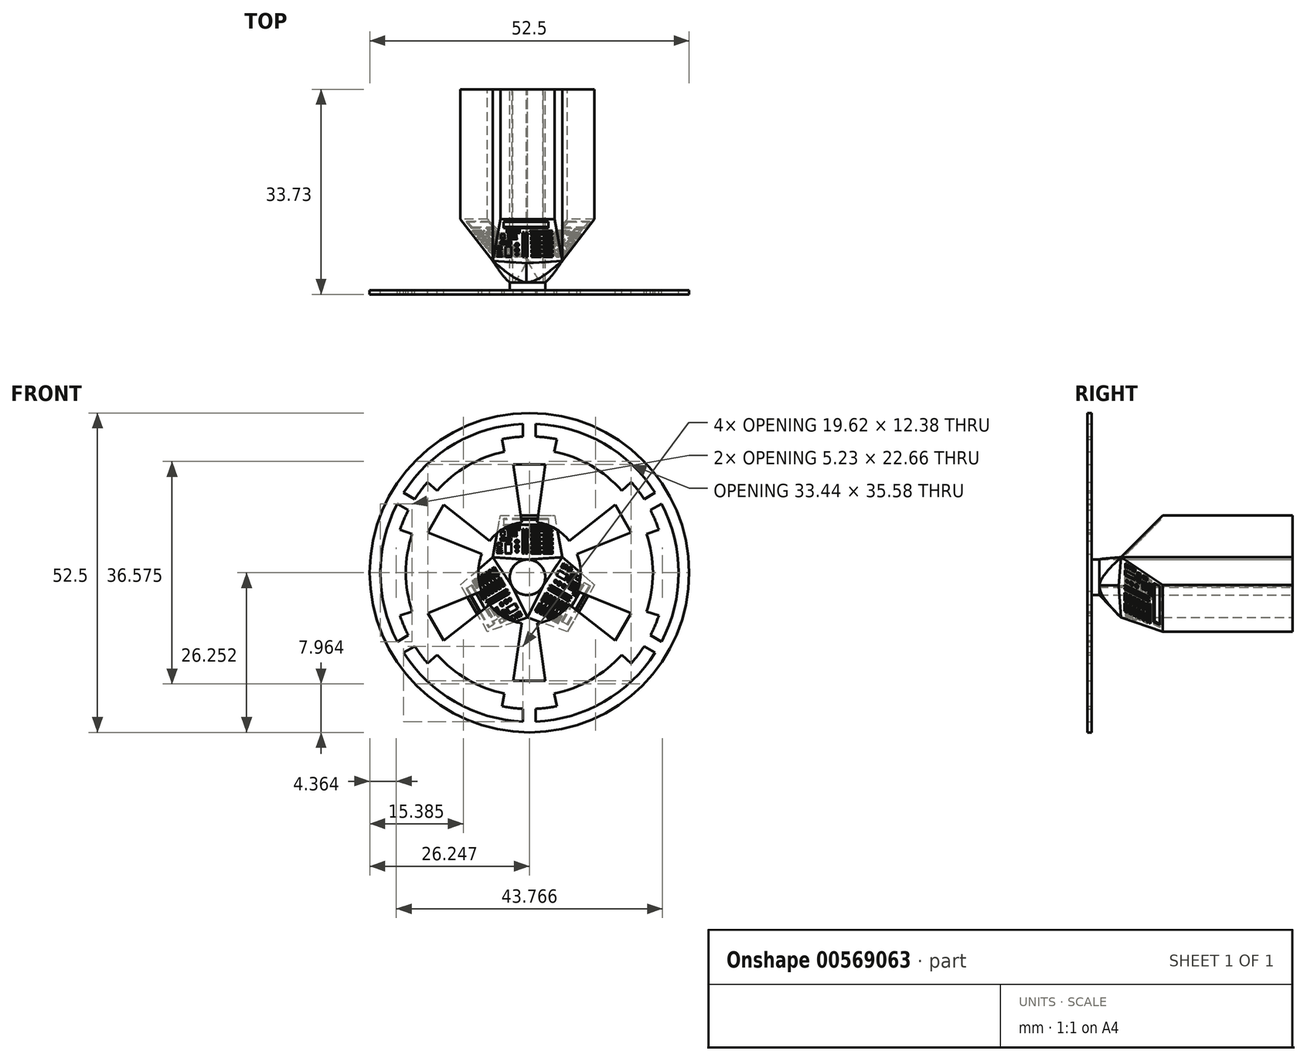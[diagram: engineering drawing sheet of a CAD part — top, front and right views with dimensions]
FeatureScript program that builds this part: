
annotation { "Feature Type Name" : "Feature", "Feature Type Description" : "" }
export const myFeature = defineFeature(function(context is Context, id is Id, definition is map)
    precondition{}
    {
        {
            var Q0;
            Q0=qCreatedBy(makeId("Front.planeOp"),FACE);
            var sketch = newSketch(context, id + "F0", { "sketchPlane" : qUnion([Q0])});
            skLineSegment(sketch, "E0", {"start": v(-5.73, 3.3) * mm, "end": v(-4.45, 10.16) * mm});
            skLineSegment(sketch, "E1", {"start": v(-4.45, 10.16) * mm, "end": v(0, 10.16) * mm});
            skLineSegment(sketch, "E2", {"start": v(0, 10.16) * mm, "end": v(4.45, 10.16) * mm});
            skLineSegment(sketch, "E3", {"start": v(4.45, 10.16) * mm, "end": v(5.73, 3.3) * mm});
            skLineSegment(sketch, "E4.1.0", {"start": v(0, -6.62) * mm, "end": v(-6.57, -8.93) * mm});
            skLineSegment(sketch, "E4.1.1", {"start": v(-6.57, -8.93) * mm, "end": v(-8.8, -5.08) * mm});
            skLineSegment(sketch, "E4.1.2", {"start": v(-8.8, -5.08) * mm, "end": v(-11.02, -1.23) * mm});
            skLineSegment(sketch, "E4.1.3", {"start": v(-11.02, -1.23) * mm, "end": v(-5.73, 3.3) * mm});
            skLineSegment(sketch, "E4.2.0", {"start": v(5.73, 3.3) * mm, "end": v(11.02, -1.23) * mm});
            skLineSegment(sketch, "E4.2.1", {"start": v(11.02, -1.23) * mm, "end": v(8.8, -5.08) * mm});
            skLineSegment(sketch, "E4.2.2", {"start": v(8.8, -5.08) * mm, "end": v(6.57, -8.93) * mm});
            skLineSegment(sketch, "E4.2.3", {"start": v(6.57, -8.93) * mm, "end": v(0, -6.62) * mm});
            skPoint(sketch, "E4.center", {"position": v(0, 0) * mm});
            skPoint(sketch, "E5.orphan", {"position": v(-3.18, 5.5) * mm});
            skPoint(sketch, "E6.end.orphan", {"position": v(-6.35, 0) * mm});
            skPoint(sketch, "E7.orphan", {"position": v(-3.18, -5.5) * mm});
            skPoint(sketch, "E8.orphan", {"position": v(3.17, 5.5) * mm});
            skPoint(sketch, "E9.orphan", {"position": v(6.35, 0) * mm});
            skCircle(sketch, "E10", {"center": v(0, 0) * mm, "radius": 2.92 * mm});
            skLineSegment(sketch, "E11", {"start": v(-5.73, 3.3) * mm, "end": v(-2.43, -1.63) * mm});
            skLineSegment(sketch, "E12", {"start": v(-2.43, -1.63) * mm, "end": v(0, -6.62) * mm});
            skLineSegment(sketch, "E13", {"start": v(0, -6.62) * mm, "end": v(2.62, -1.29) * mm});
            skLineSegment(sketch, "E14", {"start": v(2.62, -1.29) * mm, "end": v(5.73, 3.3) * mm});
            skLineSegment(sketch, "E15", {"start": v(5.73, 3.3) * mm, "end": v(0, 2.93) * mm});
            skLineSegment(sketch, "E16", {"start": v(0, 2.93) * mm, "end": v(-5.73, 3.3) * mm});
            skSolve(sketch);
        }
        {
            var Q0;
            {var subQ0=sQuery(id+"F0.wireOp",EDGE,"E10");var subQ1=makeQuery(id+"F0.imprint","INTERSECT",VERTEX,{"derivedFrom":[subQ0,sQuery(id+"F0.wireOp",EDGE,"E11"),sQuery(id+"F0.wireOp",EDGE,"E12")]});Q0=makeQuery(id+"F0.imprint","IMPRINT",FACE,{"disambiguationData":[TD([[makeQuery(id+"F0.imprint","IMPRINT",EDGE,{"disambiguationData":[TD([[subQ1,-1.0]])],"derivedFrom":subQ0}),1.0]])]});}
            extrude(context, id + "F1", {"entities" : qUnion([Q0]), "depth" : 33.02 * mm, "offsetDistance" : 25.4 * mm});
        }
        {
            var Q0;
            {var subQ0=sQuery(id+"F0.wireOp",EDGE,"E12");Q0=makeQuery(id+"F0.imprint","IMPRINT",FACE,{"disambiguationData":[TD([[makeQuery(id+"F0.imprint","IMPRINT",EDGE,{"derivedFrom":subQ0}),1.0]])]});}
            extrude(context, id + "F2", {"entities" : qUnion([Q0]), "depth" : 31.75 * mm, "offsetDistance" : 25.4 * mm});
        }
        {
            var Q0;
            Q0=makeQuery(id+"F0.imprint","IMPRINT",FACE,{"disambiguationData":[TD([[makeQuery(id+"F0.imprint","IMPRINT",EDGE,{"derivedFrom":sQuery(id+"F0.wireOp",EDGE,"E0")}),-1.0]])]});
            extrude(context, id + "F3", {"entities" : qUnion([Q0]), "depth" : 28.57 * mm, "offsetDistance" : 25.4 * mm});
        }
        {
            var Q0;
            Q0=makeQuery(id+"F3.opExtrude","CAP_EDGE",EDGE,{"disambiguationData":[OSD([sQuery(id+"F0.wireOp",EDGE,"E1"),sQuery(id+"F0.wireOp",EDGE,"E2")])],"isStart":false});
            cPoint(context, id + "F4", {"entities" : qUnion([Q0]), "parameter" : 0.5});
        }
        {
            var Q0;
            Q0=makeQuery(id+"F3.opExtrude","CAP_VERTEX",VERTEX,{"disambiguationData":[OSD([sQuery(id+"F0.wireOp",EDGE,"E15"),sQuery(id+"F0.wireOp",EDGE,"E16")])],"isStart":false});
            var Q1;
            Q1 = qCreatedBy(id + "F4" ,VERTEX);
            var Q2;
            Q2=sQuery(id+"F0.wireOp",VERTEX,"E15.end");
            cPlane(context, id + "F5", {"entities" : qUnion([Q0, Q1, Q2]), "cplaneType" : CPlaneType.THREE_POINT, "offset" : 25.4 * mm, "width" : 152.4 * mm, "height" : 152.4 * mm});
        }
        {
            var Q0;
            Q0=qCreatedBy(id+"F5.planeOp",FACE);
            var sketch = newSketch(context, id + "F6", { "sketchPlane" : qUnion([Q0])});
            skLineSegment(sketch, "E17", {"start": v(-28.58, 2.93) * mm, "end": v(-28.58, 10.16) * mm});
            skLineSegment(sketch, "E18", {"start": v(-28.58, 10.16) * mm, "end": v(-21.34, 10.16) * mm});
            skLineSegment(sketch, "E19", {"start": v(-21.34, 10.16) * mm, "end": v(-28.58, 2.93) * mm});
            skSolve(sketch);
        }
        {
            var Q0;
            Q0 = qSketchRegion(id + "F6", true);
            extrude(context, id + "F7", {"entities" : qUnion([Q0]), "operationType" : NewBodyOperationType.REMOVE, "endBound" : BoundingType.SYMMETRIC, "oppositeDirection" : true, "depth" : 25.4 * mm, "offsetDistance" : 25.4 * mm});
        }
        {
            var Q0;
            Q0=makeQuery(id+"F7.boolean.opBoolean","COPY",FACE,{"derivedFrom":makeQuery(id+"F7.opExtrude","SWEPT_FACE",FACE,{"disambiguationData":[OSD([sQuery(id+"F6.wireOp",EDGE,"E19")])]})});
            var sketch = newSketch(context, id + "F8", { "sketchPlane" : qUnion([Q0])});
            skLineSegment(sketch, "E20.bottom", {"start": v(4.16, -16.74) * mm, "end": v(2.61, -16.74) * mm});
            skLineSegment(sketch, "E20.top", {"start": v(4.16, -16.07) * mm, "end": v(2.61, -16.07) * mm});
            skLineSegment(sketch, "E20.left", {"start": v(4.16, -16.74) * mm, "end": v(4.16, -16.07) * mm});
            skLineSegment(sketch, "E20.right", {"start": v(2.61, -16.74) * mm, "end": v(2.61, -16.07) * mm});
            skLineSegment(sketch, "E21.bottom", {"start": v(-2.69, -16.71) * mm, "end": v(-3.61, -16.71) * mm});
            skLineSegment(sketch, "E21.top", {"start": v(-2.69, -14.27) * mm, "end": v(-3.61, -14.27) * mm});
            skLineSegment(sketch, "E21.left", {"start": v(-2.69, -16.71) * mm, "end": v(-2.69, -14.27) * mm});
            skLineSegment(sketch, "E21.right", {"start": v(-3.61, -16.71) * mm, "end": v(-3.61, -14.27) * mm});
            skCircle(sketch, "E22", {"center": v(-1.84, -12.51) * mm, "radius": 0.13 * mm});
            skLineSegment(sketch, "E23.1.0.0", {"start": v(4.14, -15.75) * mm, "end": v(2.6, -15.75) * mm});
            skLineSegment(sketch, "E23.1.0.1", {"start": v(2.6, -15.75) * mm, "end": v(2.6, -15.07) * mm});
            skLineSegment(sketch, "E23.1.0.2", {"start": v(4.14, -15.07) * mm, "end": v(2.6, -15.07) * mm});
            skLineSegment(sketch, "E23.1.0.3", {"start": v(4.14, -15.75) * mm, "end": v(4.14, -15.07) * mm});
            skLineSegment(sketch, "E23.2.0.0", {"start": v(4.12, -14.75) * mm, "end": v(2.57, -14.75) * mm});
            skLineSegment(sketch, "E23.2.0.1", {"start": v(2.57, -14.75) * mm, "end": v(2.57, -14.08) * mm});
            skLineSegment(sketch, "E23.2.0.2", {"start": v(4.12, -14.08) * mm, "end": v(2.57, -14.08) * mm});
            skLineSegment(sketch, "E23.2.0.3", {"start": v(4.12, -14.75) * mm, "end": v(4.12, -14.08) * mm});
            skLineSegment(sketch, "E23.3.0.0", {"start": v(4.1, -13.76) * mm, "end": v(2.55, -13.76) * mm});
            skLineSegment(sketch, "E23.3.0.1", {"start": v(2.55, -13.76) * mm, "end": v(2.55, -13.08) * mm});
            skLineSegment(sketch, "E23.3.0.2", {"start": v(4.1, -13.08) * mm, "end": v(2.55, -13.08) * mm});
            skLineSegment(sketch, "E23.3.0.3", {"start": v(4.1, -13.76) * mm, "end": v(4.1, -13.08) * mm});
            skLineSegment(sketch, "E23.4.0.0", {"start": v(4.09, -12.77) * mm, "end": v(2.53, -12.77) * mm});
            skLineSegment(sketch, "E23.4.0.1", {"start": v(2.53, -12.77) * mm, "end": v(2.53, -12.1) * mm});
            skLineSegment(sketch, "E23.4.0.2", {"start": v(4.09, -12.1) * mm, "end": v(2.53, -12.1) * mm});
            skLineSegment(sketch, "E23.4.0.3", {"start": v(4.09, -12.77) * mm, "end": v(4.09, -12.1) * mm});
            skLineSegment(sketch, "E23.direction1", {"start": v(2.61, -16.74) * mm, "end": v(2.6, -15.75) * mm, "construction": true});
            skLineSegment(sketch, "E24.1.0.0", {"start": v(0.58, -12.76) * mm, "end": v(0.58, -12.09) * mm});
            skLineSegment(sketch, "E24.1.0.1", {"start": v(2.14, -12.09) * mm, "end": v(0.58, -12.09) * mm});
            skLineSegment(sketch, "E24.1.0.2", {"start": v(0.64, -15.74) * mm, "end": v(0.64, -15.07) * mm});
            skLineSegment(sketch, "E24.1.0.3", {"start": v(2.2, -15.74) * mm, "end": v(2.2, -15.07) * mm});
            skLineSegment(sketch, "E24.1.0.4", {"start": v(2.21, -16.74) * mm, "end": v(2.21, -16.06) * mm});
            skLineSegment(sketch, "E24.1.0.5", {"start": v(2.2, -15.07) * mm, "end": v(0.64, -15.07) * mm});
            skLineSegment(sketch, "E24.1.0.6", {"start": v(2.21, -16.06) * mm, "end": v(0.66, -16.06) * mm});
            skLineSegment(sketch, "E24.1.0.7", {"start": v(0.66, -16.74) * mm, "end": v(0.64, -15.74) * mm, "construction": true});
            skLineSegment(sketch, "E24.1.0.8", {"start": v(2.21, -16.74) * mm, "end": v(0.66, -16.74) * mm});
            skLineSegment(sketch, "E24.1.0.9", {"start": v(2.17, -14.75) * mm, "end": v(2.17, -14.08) * mm});
            skLineSegment(sketch, "E24.1.0.10", {"start": v(2.15, -13.08) * mm, "end": v(0.6, -13.08) * mm});
            skLineSegment(sketch, "E24.1.0.11", {"start": v(2.17, -14.75) * mm, "end": v(0.62, -14.75) * mm});
            skLineSegment(sketch, "E24.1.0.12", {"start": v(2.15, -13.76) * mm, "end": v(0.6, -13.76) * mm});
            skLineSegment(sketch, "E24.1.0.13", {"start": v(0.62, -14.75) * mm, "end": v(0.62, -14.08) * mm});
            skLineSegment(sketch, "E24.1.0.14", {"start": v(2.15, -13.76) * mm, "end": v(2.15, -13.08) * mm});
            skLineSegment(sketch, "E24.1.0.15", {"start": v(2.14, -12.76) * mm, "end": v(0.58, -12.76) * mm});
            skLineSegment(sketch, "E24.1.0.16", {"start": v(2.14, -12.76) * mm, "end": v(2.14, -12.09) * mm});
            skLineSegment(sketch, "E24.1.0.17", {"start": v(2.17, -14.08) * mm, "end": v(0.62, -14.08) * mm});
            skLineSegment(sketch, "E24.1.0.18", {"start": v(0.6, -13.76) * mm, "end": v(0.6, -13.08) * mm});
            skLineSegment(sketch, "E24.1.0.19", {"start": v(2.2, -15.74) * mm, "end": v(0.64, -15.74) * mm});
            skLineSegment(sketch, "E24.1.0.20", {"start": v(0.66, -16.74) * mm, "end": v(0.66, -16.06) * mm});
            skLineSegment(sketch, "E24.direction1", {"start": v(2.61, -16.74) * mm, "end": v(0.66, -16.74) * mm, "construction": true});
            skCircle(sketch, "E25.1.0.0", {"center": v(-2.15, -12.52) * mm, "radius": 0.13 * mm});
            skCircle(sketch, "E25.2.0.0", {"center": v(-2.46, -12.52) * mm, "radius": 0.13 * mm});
            skCircle(sketch, "E25.3.0.0", {"center": v(-2.76, -12.52) * mm, "radius": 0.13 * mm});
            skCircle(sketch, "E25.4.0.0", {"center": v(-3.07, -12.52) * mm, "radius": 0.13 * mm});
            skLineSegment(sketch, "E25.direction1", {"start": v(-1.84, -12.51) * mm, "end": v(-2.15, -12.52) * mm, "construction": true});
            skCircle(sketch, "E26.1.0.0", {"center": v(-2.8, -12.14) * mm, "radius": 0.13 * mm});
            skCircle(sketch, "E26.1.0.1", {"center": v(-2.18, -12.13) * mm, "radius": 0.13 * mm});
            skCircle(sketch, "E26.1.0.2", {"center": v(-2.48, -12.14) * mm, "radius": 0.13 * mm});
            skCircle(sketch, "E26.1.0.3", {"center": v(-1.87, -12.13) * mm, "radius": 0.13 * mm});
            skLineSegment(sketch, "E26.1.0.4", {"start": v(-1.87, -12.13) * mm, "end": v(-2.18, -12.13) * mm, "construction": true});
            skCircle(sketch, "E26.1.0.5", {"center": v(-3.1, -12.14) * mm, "radius": 0.13 * mm});
            skCircle(sketch, "E26.2.0.0", {"center": v(-2.82, -11.76) * mm, "radius": 0.13 * mm});
            skCircle(sketch, "E26.2.0.1", {"center": v(-2.2, -11.75) * mm, "radius": 0.13 * mm});
            skCircle(sketch, "E26.2.0.2", {"center": v(-2.5, -11.75) * mm, "radius": 0.13 * mm});
            skCircle(sketch, "E26.2.0.3", {"center": v(-1.9, -11.75) * mm, "radius": 0.13 * mm});
            skLineSegment(sketch, "E26.2.0.4", {"start": v(-1.9, -11.75) * mm, "end": v(-2.2, -11.75) * mm, "construction": true});
            skCircle(sketch, "E26.2.0.5", {"center": v(-3.13, -11.76) * mm, "radius": 0.13 * mm});
            skLineSegment(sketch, "E26.direction1", {"start": v(-3.07, -12.52) * mm, "end": v(-3.1, -12.14) * mm, "construction": true});
            skLineSegment(sketch, "E27.bottom", {"start": v(0, -16.72) * mm, "end": v(-0.28, -16.72) * mm});
            skLineSegment(sketch, "E27.top", {"start": v(0, -11.05) * mm, "end": v(-0.28, -11.05) * mm});
            skLineSegment(sketch, "E27.left", {"start": v(0, -16.72) * mm, "end": v(0, -11.05) * mm});
            skLineSegment(sketch, "E27.right", {"start": v(-0.28, -16.72) * mm, "end": v(-0.28, -11.05) * mm});
            skLineSegment(sketch, "E28.bottom", {"start": v(-0.56, -16.73) * mm, "end": v(-0.84, -16.73) * mm});
            skLineSegment(sketch, "E28.top", {"start": v(-0.56, -11.05) * mm, "end": v(-0.84, -11.05) * mm});
            skLineSegment(sketch, "E28.left", {"start": v(-0.56, -16.73) * mm, "end": v(-0.56, -11.05) * mm});
            skLineSegment(sketch, "E28.right", {"start": v(-0.84, -16.73) * mm, "end": v(-0.84, -11.05) * mm});
            skLineSegment(sketch, "E29.bottom", {"start": v(4.1, -11.55) * mm, "end": v(0.43, -11.55) * mm});
            skLineSegment(sketch, "E29.top", {"start": v(4.1, -11.28) * mm, "end": v(0.43, -11.28) * mm});
            skLineSegment(sketch, "E29.left", {"start": v(4.1, -11.55) * mm, "end": v(4.1, -11.28) * mm});
            skLineSegment(sketch, "E29.right", {"start": v(0.43, -11.55) * mm, "end": v(0.43, -11.28) * mm});
            skLineSegment(sketch, "E30.bottom", {"start": v(4.05, -10.93) * mm, "end": v(0.42, -10.93) * mm});
            skLineSegment(sketch, "E30.top", {"start": v(4.05, -10.71) * mm, "end": v(0.42, -10.71) * mm});
            skLineSegment(sketch, "E30.left", {"start": v(4.05, -10.93) * mm, "end": v(4.05, -10.71) * mm});
            skLineSegment(sketch, "E30.right", {"start": v(0.42, -10.93) * mm, "end": v(0.42, -10.71) * mm});
            skCircle(sketch, "E31", {"center": v(-1.73, -16.14) * mm, "radius": 0.25 * mm});
            skCircle(sketch, "E32", {"center": v(-1.71, -15.13) * mm, "radius": 0.36 * mm});
            skCircle(sketch, "E33", {"center": v(-1.73, -13.91) * mm, "radius": 0.34 * mm});
            skLineSegment(sketch, "E34.bottom", {"start": v(-4.15, -16.61) * mm, "end": v(-5, -16.61) * mm});
            skLineSegment(sketch, "E34.top", {"start": v(-4.15, -16.35) * mm, "end": v(-5, -16.35) * mm});
            skLineSegment(sketch, "E34.left", {"start": v(-4.15, -16.61) * mm, "end": v(-4.15, -16.35) * mm});
            skLineSegment(sketch, "E34.right", {"start": v(-5, -16.61) * mm, "end": v(-5, -16.35) * mm});
            skLineSegment(sketch, "E35.bottom", {"start": v(-4.18, -16.14) * mm, "end": v(-4.98, -16.14) * mm});
            skLineSegment(sketch, "E35.top", {"start": v(-4.18, -15.9) * mm, "end": v(-4.98, -15.9) * mm});
            skLineSegment(sketch, "E35.left", {"start": v(-4.18, -16.14) * mm, "end": v(-4.18, -15.9) * mm});
            skLineSegment(sketch, "E35.right", {"start": v(-4.98, -16.14) * mm, "end": v(-4.98, -15.9) * mm});
            skLineSegment(sketch, "E36.bottom", {"start": v(-4.24, -15.63) * mm, "end": v(-5.01, -15.63) * mm});
            skLineSegment(sketch, "E36.top", {"start": v(-4.24, -15.45) * mm, "end": v(-5.01, -15.45) * mm});
            skLineSegment(sketch, "E36.left", {"start": v(-4.24, -15.63) * mm, "end": v(-4.24, -15.45) * mm});
            skLineSegment(sketch, "E36.right", {"start": v(-5.01, -15.63) * mm, "end": v(-5.01, -15.45) * mm});
            skLineSegment(sketch, "E37.bottom", {"start": v(-4.23, -15.14) * mm, "end": v(-4.93, -15.14) * mm});
            skLineSegment(sketch, "E37.top", {"start": v(-4.23, -14.22) * mm, "end": v(-4.93, -14.22) * mm});
            skLineSegment(sketch, "E37.left", {"start": v(-4.23, -15.14) * mm, "end": v(-4.23, -14.22) * mm});
            skLineSegment(sketch, "E37.right", {"start": v(-4.93, -15.14) * mm, "end": v(-4.93, -14.22) * mm});
            skLineSegment(sketch, "E38.bottom", {"start": v(3.45, -8.6) * mm, "end": v(-3.9, -8.6) * mm});
            skLineSegment(sketch, "E38.top", {"start": v(3.45, -10.02) * mm, "end": v(-3.9, -10.02) * mm});
            skLineSegment(sketch, "E38.left", {"start": v(3.45, -8.6) * mm, "end": v(3.45, -10.02) * mm});
            skLineSegment(sketch, "E38.right", {"start": v(-3.9, -8.6) * mm, "end": v(-3.9, -10.02) * mm});
            skLineSegment(sketch, "E39.bottom", {"start": v(-3.77, -12.52) * mm, "end": v(-4.38, -12.52) * mm});
            skLineSegment(sketch, "E39.top", {"start": v(-3.77, -11.43) * mm, "end": v(-4.38, -11.43) * mm});
            skLineSegment(sketch, "E39.left", {"start": v(-3.77, -12.52) * mm, "end": v(-3.77, -11.43) * mm});
            skLineSegment(sketch, "E39.right", {"start": v(-4.38, -12.52) * mm, "end": v(-4.38, -11.43) * mm});
            skLineSegment(sketch, "E40.bottom", {"start": v(-1.29, -10.31) * mm, "end": v(-3.43, -10.31) * mm});
            skLineSegment(sketch, "E40.top", {"start": v(-1.29, -11.18) * mm, "end": v(-3.43, -11.18) * mm});
            skLineSegment(sketch, "E40.left", {"start": v(-1.29, -10.31) * mm, "end": v(-1.29, -11.18) * mm});
            skLineSegment(sketch, "E40.right", {"start": v(-3.43, -10.31) * mm, "end": v(-3.43, -11.18) * mm});
            skLineSegment(sketch, "E41.bottom", {"start": v(-2.63, -13.76) * mm, "end": v(-4.45, -13.76) * mm});
            skLineSegment(sketch, "E41.top", {"start": v(-2.63, -13.07) * mm, "end": v(-4.45, -13.07) * mm});
            skLineSegment(sketch, "E41.left", {"start": v(-2.63, -13.76) * mm, "end": v(-2.63, -13.07) * mm});
            skLineSegment(sketch, "E41.right", {"start": v(-4.45, -13.76) * mm, "end": v(-4.45, -13.07) * mm});
            skSolve(sketch);
        }
        {
            var Q0;
            Q0 = qSketchRegion(id + "F8", true);
            extrude(context, id + "F9", {"entities" : qUnion([Q0]), "operationType" : NewBodyOperationType.REMOVE, "oppositeDirection" : true, "depth" : 0.25 * mm, "offsetDistance" : 25.4 * mm});
        }
        {
            var Q0;
            Q0=makeQuery(id+"F3.opExtrude","SWEPT_BODY",BODY,{"disambiguationData":[OSD([sQuery(id+"F0.wireOp",EDGE,"E0"),sQuery(id+"F0.wireOp",EDGE,"E1"),sQuery(id+"F0.wireOp",EDGE,"E2"),sQuery(id+"F0.wireOp",EDGE,"E3"),sQuery(id+"F0.wireOp",EDGE,"E15"),sQuery(id+"F0.wireOp",EDGE,"E16")])]});
            var Q1;
            Q1=makeQuery(id+"F1.opExtrude","SWEPT_BODY",BODY,{"disambiguationData":[OSD([sQuery(id+"F0.wireOp",EDGE,"E10")])]});
            var Q2;
            Q2=makeQuery(id+"F1.opExtrude","SWEPT_FACE",FACE,{"disambiguationData":[OSD([sQuery(id+"F0.wireOp",EDGE,"E10")])]});
            circularPattern(context, id + "F10", {"entities" : qUnion([Q0, Q1]), "axis" : qUnion([Q2]), "angle" : 360 * degree, "instanceCount" : 3, "equalSpace" : true});
        }
        {
            var Q0;
            Q0=makeQuery(id+"F2.opExtrude","SWEPT_BODY",BODY,{"disambiguationData":[OSD([sQuery(id+"F0.wireOp",EDGE,"E10"),sQuery(id+"F0.wireOp",EDGE,"E12"),sQuery(id+"F0.wireOp",EDGE,"E13")])]});
            var Q1;
            Q1=makeQuery(id+"F10.opPattern","COPY",FACE,{"derivedFrom":makeQuery(id+"F1.opExtrude","SWEPT_FACE",FACE,{"disambiguationData":[OSD([sQuery(id+"F0.wireOp",EDGE,"E10")])]}),"instanceName":"1"});
            circularPattern(context, id + "F11", {"entities" : qUnion([Q0]), "axis" : qUnion([Q1]), "angle" : 360 * degree, "instanceCount" : 3, "equalSpace" : true});
        }
        {
            var Q0;
            Q0=qCreatedBy(id+"F5.planeOp",FACE);
            var sketch = newSketch(context, id + "F12", { "sketchPlane" : qUnion([Q0])});
            skLineSegment(sketch, "E42", {"start": v(-31.75, -6.62) * mm, "end": v(-28.2, -6.62) * mm});
            skLineSegment(sketch, "E43", {"start": v(-28.2, -6.62) * mm, "end": v(-31.75, -2.91) * mm});
            skLineSegment(sketch, "E44", {"start": v(-31.75, -2.91) * mm, "end": v(-31.75, -6.62) * mm});
            skSolve(sketch);
        }
        {
            var Q0;
            Q0 = qSketchRegion(id + "F12", true);
            var Q1;
            Q1=makeQuery(id+"F10.opPattern","COPY",FACE,{"derivedFrom":makeQuery(id+"F1.opExtrude","SWEPT_FACE",FACE,{"disambiguationData":[OSD([sQuery(id+"F0.wireOp",EDGE,"E10")])]}),"instanceName":"1"});
            revolve(context, id + "F13", {"operationType" : NewBodyOperationType.REMOVE, "entities" : qUnion([Q0]), "axis" : qUnion([Q1]), "revolveType" : RevolveType.FULL, "oppositeDirection" : true});
        }
        {
            var Q0;
            Q0=makeQuery(id+"F1.opExtrude","CAP_FACE",FACE,{"disambiguationData":[OSD([sQuery(id+"F0.wireOp",EDGE,"E10")])],"isStart":false});
            var sketch = newSketch(context, id + "F14", { "sketchPlane" : qUnion([Q0])});
            skArc(sketch, "E45", {"start": v(0.45, 38.59) * mm, "mid": v(-35.26, 12.53) * mm, "end": v(-21.35, -29.42) * mm});
            skArc(sketch, "E46", {"start": v(-30.58, 17.27) * mm, "mid": v(-34.55, 1.09) * mm, "end": v(-30.58, -15.1) * mm});
            skLineSegment(sketch, "E47.left", {"start": v(-1.05, 36.07) * mm, "end": v(-1.05, 33.05) * mm});
            skLineSegment(sketch, "E47.right", {"start": v(1.95, 36.07) * mm, "end": v(1.95, 33.05) * mm});
            skLineSegment(sketch, "E48.1.0", {"start": v(-30.58, -15.1) * mm, "end": v(-27.98, -13.6) * mm});
            skLineSegment(sketch, "E48.1.1", {"start": v(-29.08, -17.7) * mm, "end": v(-26.48, -16.2) * mm});
            skLineSegment(sketch, "E48.2.0", {"start": v(29.99, -17.7) * mm, "end": v(27.39, -16.2) * mm});
            skLineSegment(sketch, "E48.2.1", {"start": v(31.49, -15.1) * mm, "end": v(28.89, -13.6) * mm});
            skArc(sketch, "E49", {"start": v(-27.98, 15.77) * mm, "mid": v(-28.92, 13.8) * mm, "end": v(-29.72, 11.75) * mm});
            skArc(sketch, "E50", {"start": v(-27.07, 10.22) * mm, "mid": v(-28.55, 1.09) * mm, "end": v(-27.07, -8.05) * mm});
            skPoint(sketch, "E51.orphan", {"position": v(-31.47, 17.79) * mm});
            skPoint(sketch, "E52.orphan", {"position": v(-29.97, 20.39) * mm});
            skPoint(sketch, "E53.orphan", {"position": v(-27.8, 24.15) * mm});
            skLineSegment(sketch, "E54.trimOffspring", {"start": v(-26.48, 18.37) * mm, "end": v(-29.08, 19.87) * mm});
            skLineSegment(sketch, "E55.trimOffspring", {"start": v(-27.98, 15.77) * mm, "end": v(-30.58, 17.27) * mm});
            skArc(sketch, "E56.trimOffspring", {"start": v(-29.72, -9.58) * mm, "mid": v(-28.92, -11.62) * mm, "end": v(-27.98, -13.6) * mm});
            skArc(sketch, "E57.trimOffspring", {"start": v(-23.87, 21.88) * mm, "mid": v(-25.23, 20.17) * mm, "end": v(-26.48, 18.37) * mm});
            skPoint(sketch, "E58.orphan", {"position": v(-5.4, 37.09) * mm});
            skPoint(sketch, "E59.orphan", {"position": v(1.95, 37.09) * mm});
            skPoint(sketch, "E60.orphan", {"position": v(-1.05, 37.09) * mm});
            skPoint(sketch, "E61.orphan", {"position": v(6.3, 37.09) * mm});
            skArc(sketch, "E62.trimOffspring", {"start": v(-21.35, -29.42) * mm, "mid": v(36.16, -10.36) * mm, "end": v(0.45, 38.59) * mm});
            skArc(sketch, "E63.trimOffspring", {"start": v(6.3, 32.55) * mm, "mid": v(4.14, 32.88) * mm, "end": v(1.95, 33.05) * mm});
            skArc(sketch, "E64.trimOffspring", {"start": v(-5.4, 29.5) * mm, "mid": v(-14.05, 26.2) * mm, "end": v(-21.22, 20.36) * mm});
            skArc(sketch, "E65.trimOffspring", {"start": v(-1.05, 36.06) * mm, "mid": v(-17.05, 31.4) * mm, "end": v(-29.08, 19.87) * mm});
            skArc(sketch, "E66.trimOffspring", {"start": v(-1.05, 33.05) * mm, "mid": v(-3.23, 32.88) * mm, "end": v(-5.4, 32.55) * mm});
            skArc(sketch, "E67.trimOffspring", {"start": v(22.13, 20.36) * mm, "mid": v(14.95, 26.2) * mm, "end": v(6.3, 29.5) * mm});
            skPoint(sketch, "E68.orphan", {"position": v(30.88, 20.39) * mm});
            skPoint(sketch, "E69.orphan", {"position": v(32.38, 17.79) * mm});
            skPoint(sketch, "E70.orphan", {"position": v(34.55, 14.02) * mm});
            skLineSegment(sketch, "E71.trimOffspring", {"start": v(27.39, 18.37) * mm, "end": v(29.99, 19.87) * mm});
            skLineSegment(sketch, "E72.trimOffspring", {"start": v(28.89, 15.77) * mm, "end": v(31.49, 17.27) * mm});
            skArc(sketch, "E73.trimOffspring", {"start": v(27.39, 18.37) * mm, "mid": v(26.14, 20.17) * mm, "end": v(24.77, 21.88) * mm});
            skArc(sketch, "E74.trimOffspring", {"start": v(29.99, 19.87) * mm, "mid": v(17.95, 31.4) * mm, "end": v(1.95, 36.06) * mm});
            skArc(sketch, "E75.trimOffspring", {"start": v(30.62, 11.75) * mm, "mid": v(29.82, 13.8) * mm, "end": v(28.89, 15.77) * mm});
            skPoint(sketch, "E76.orphan", {"position": v(34.55, -11.85) * mm});
            skArc(sketch, "E77.trimOffspring", {"start": v(27.98, -8.05) * mm, "mid": v(29.45, 1.09) * mm, "end": v(27.98, 10.22) * mm});
            skArc(sketch, "E78.trimOffspring", {"start": v(28.89, -13.6) * mm, "mid": v(29.82, -11.62) * mm, "end": v(30.62, -9.58) * mm});
            skPoint(sketch, "E79.orphan", {"position": v(32.38, -15.61) * mm});
            skPoint(sketch, "E80.orphan", {"position": v(30.88, -18.21) * mm});
            skArc(sketch, "E81.trimOffspring", {"start": v(24.77, -19.7) * mm, "mid": v(26.14, -18) * mm, "end": v(27.39, -16.2) * mm});
            skArc(sketch, "E82.trimOffspring", {"start": v(6.3, -27.32) * mm, "mid": v(14.95, -24.03) * mm, "end": v(22.13, -18.18) * mm});
            skLineSegment(sketch, "E83.trimOffspring", {"start": v(-1.05, -30.88) * mm, "end": v(-1.05, -33.9) * mm});
            skLineSegment(sketch, "E84.trimOffspring", {"start": v(1.95, -30.88) * mm, "end": v(1.95, -33.88) * mm});
            skArc(sketch, "E85.trimOffspring", {"start": v(1.95, -30.88) * mm, "mid": v(4.14, -30.7) * mm, "end": v(6.3, -30.37) * mm});
            skPoint(sketch, "E86.orphan", {"position": v(6.3, -34.91) * mm});
            skArc(sketch, "E87.trimOffspring", {"start": v(1.95, -33.88) * mm, "mid": v(17.95, -29.22) * mm, "end": v(29.99, -17.7) * mm});
            skPoint(sketch, "E88.orphan", {"position": v(-1.05, -34.91) * mm});
            skPoint(sketch, "E89.trimOffspring.end.orphan", {"position": v(-5.4, -34.91) * mm});
            skPoint(sketch, "E90.top.end.orphan", {"position": v(1.95, -34.91) * mm});
            skPoint(sketch, "E91.orphan", {"position": v(-33.65, -11.85) * mm});
            skPoint(sketch, "E92.orphan", {"position": v(-31.47, -15.61) * mm});
            skPoint(sketch, "E93.orphan", {"position": v(-29.97, -18.21) * mm});
            skPoint(sketch, "E94.orphan", {"position": v(-27.8, -21.98) * mm});
            skArc(sketch, "E95.trimOffspring", {"start": v(-29.08, -17.7) * mm, "mid": v(-17.05, -29.22) * mm, "end": v(-1.05, -33.88) * mm});
            skArc(sketch, "E96.trimOffspring", {"start": v(-26.48, -16.2) * mm, "mid": v(-25.23, -18) * mm, "end": v(-23.87, -19.7) * mm});
            skArc(sketch, "E97.trimOffspring", {"start": v(-21.22, -18.18) * mm, "mid": v(-14.05, -24.03) * mm, "end": v(-5.4, -27.32) * mm});
            skArc(sketch, "E98", {"start": v(-1.37, 12.95) * mm, "mid": v(-5.55, 11.48) * mm, "end": v(-8.9, 8.6) * mm});
            skLineSegment(sketch, "E99.bottom", {"start": v(-3.3, 26.5) * mm, "end": v(4.2, 26.5) * mm});
            skLineSegment(sketch, "E99.top", {"start": v(-3.3, -24.33) * mm, "end": v(4.2, -24.33) * mm});
            skLineSegment(sketch, "E100", {"start": v(-3.3, 26.5) * mm, "end": v(-1.37, 12.95) * mm});
            skLineSegment(sketch, "E101", {"start": v(4.2, 26.5) * mm, "end": v(2.27, 12.95) * mm});
            skLineSegment(sketch, "E102", {"start": v(-3.3, -24.33) * mm, "end": v(-1.37, -10.77) * mm});
            skLineSegment(sketch, "E103", {"start": v(4.2, -24.33) * mm, "end": v(2.27, -10.77) * mm});
            skLineSegment(sketch, "E104.1.0", {"start": v(-19.68, -14.87) * mm, "end": v(-23.43, -8.37) * mm});
            skLineSegment(sketch, "E104.1.1", {"start": v(-23.43, -8.37) * mm, "end": v(-10.73, -3.27) * mm});
            skLineSegment(sketch, "E104.1.2", {"start": v(-19.68, -14.87) * mm, "end": v(-8.9, -6.42) * mm});
            skLineSegment(sketch, "E104.1.3", {"start": v(24.34, 10.55) * mm, "end": v(20.59, 17.05) * mm});
            skLineSegment(sketch, "E104.1.4", {"start": v(20.59, 17.05) * mm, "end": v(9.81, 8.6) * mm});
            skLineSegment(sketch, "E104.1.5", {"start": v(24.34, 10.55) * mm, "end": v(11.64, 5.44) * mm});
            skLineSegment(sketch, "E104.2.0", {"start": v(24.34, -8.37) * mm, "end": v(20.59, -14.86) * mm});
            skLineSegment(sketch, "E104.2.1", {"start": v(20.59, -14.86) * mm, "end": v(9.81, -6.42) * mm});
            skLineSegment(sketch, "E104.2.2", {"start": v(24.34, -8.37) * mm, "end": v(11.64, -3.27) * mm});
            skLineSegment(sketch, "E104.2.3", {"start": v(-19.68, 17.04) * mm, "end": v(-23.43, 10.55) * mm});
            skLineSegment(sketch, "E104.2.4", {"start": v(-23.43, 10.55) * mm, "end": v(-10.73, 5.44) * mm});
            skLineSegment(sketch, "E104.2.5", {"start": v(-19.68, 17.04) * mm, "end": v(-8.9, 8.6) * mm});
            skArc(sketch, "E105.trimOffspring", {"start": v(9.81, 8.6) * mm, "mid": v(6.45, 11.48) * mm, "end": v(2.27, 12.95) * mm});
            skArc(sketch, "E106.trimOffspring", {"start": v(11.64, -3.27) * mm, "mid": v(12.45, 1.09) * mm, "end": v(11.64, 5.44) * mm});
            skArc(sketch, "E107.trimOffspring", {"start": v(2.27, -10.77) * mm, "mid": v(6.45, -9.3) * mm, "end": v(9.81, -6.42) * mm});
            skArc(sketch, "E108.trimOffspring", {"start": v(-8.9, -6.42) * mm, "mid": v(-5.55, -9.3) * mm, "end": v(-1.37, -10.77) * mm});
            skArc(sketch, "E109.trimOffspring", {"start": v(-10.73, 5.44) * mm, "mid": v(-11.55, 1.09) * mm, "end": v(-10.73, -3.27) * mm});
            skLineSegment(sketch, "E110", {"start": v(6.9, 32.43) * mm, "end": v(6.3, 29.5) * mm});
            skLineSegment(sketch, "E111", {"start": v(-6, 32.43) * mm, "end": v(-5.4, 29.5) * mm});
            skLineSegment(sketch, "E112", {"start": v(24.37, -20.17) * mm, "end": v(22.13, -18.18) * mm});
            skLineSegment(sketch, "E113", {"start": v(-29.92, 11.17) * mm, "end": v(-27.07, 10.22) * mm});
            skLineSegment(sketch, "E114", {"start": v(30.82, 11.17) * mm, "end": v(27.98, 10.22) * mm});
            skLineSegment(sketch, "E115", {"start": v(-23.46, -20.17) * mm, "end": v(-21.22, -18.18) * mm});
            skArc(sketch, "E116.converted", {"start": v(-6, -30.25) * mm, "mid": v(-3.54, -30.66) * mm, "end": v(-1.05, -30.88) * mm});
            skArc(sketch, "E117.trimOffspring", {"start": v(24.37, -20.17) * mm, "mid": v(25.95, -18.24) * mm, "end": v(27.39, -16.2) * mm});
            skLineSegment(sketch, "E118.trimOffspring", {"start": v(-5.4, -27.32) * mm, "end": v(-6.04, -30.43) * mm});
            skLineSegment(sketch, "E119.trimOffspring", {"start": v(6.3, -27.32) * mm, "end": v(6.9, -30.25) * mm});
            skArc(sketch, "E120.trimOffspring", {"start": v(30.82, 11.17) * mm, "mid": v(29.94, 13.5) * mm, "end": v(28.89, 15.77) * mm});
            skLineSegment(sketch, "E121.trimOffspring", {"start": v(27.98, -8.05) * mm, "end": v(30.82, -9) * mm});
            skLineSegment(sketch, "E122.trimOffspring", {"start": v(22.13, 20.36) * mm, "end": v(24.37, 22.35) * mm});
            skArc(sketch, "E123.trimOffspring", {"start": v(6.9, 32.43) * mm, "mid": v(4.44, 32.84) * mm, "end": v(1.95, 33.05) * mm});
            skArc(sketch, "E124.trimOffspring", {"start": v(-23.46, 22.35) * mm, "mid": v(-25.05, 20.42) * mm, "end": v(-26.48, 18.37) * mm});
            skLineSegment(sketch, "E125.trimOffspring", {"start": v(-21.22, 20.36) * mm, "end": v(-23.46, 22.35) * mm});
            skArc(sketch, "E126.trimOffspring", {"start": v(-29.92, -9) * mm, "mid": v(-29.04, -11.33) * mm, "end": v(-27.98, -13.6) * mm});
            skLineSegment(sketch, "E127.trimOffspring", {"start": v(-27.07, -8.05) * mm, "end": v(-29.92, -9) * mm});
            skArc(sketch, "E128.trimOffspring", {"start": v(1.95, -30.88) * mm, "mid": v(4.44, -30.66) * mm, "end": v(6.9, -30.25) * mm});
            skArc(sketch, "E129.trimOffspring", {"start": v(28.89, -13.6) * mm, "mid": v(29.94, -11.33) * mm, "end": v(30.82, -9) * mm});
            skArc(sketch, "E130.trimOffspring", {"start": v(27.39, 18.37) * mm, "mid": v(25.95, 20.42) * mm, "end": v(24.37, 22.35) * mm});
            skArc(sketch, "E131.trimOffspring", {"start": v(-1.05, 33.05) * mm, "mid": v(-3.54, 32.84) * mm, "end": v(-6, 32.43) * mm});
            skArc(sketch, "E132.trimOffspring", {"start": v(-27.98, 15.77) * mm, "mid": v(-29.04, 13.5) * mm, "end": v(-29.92, 11.17) * mm});
            skArc(sketch, "E133.trimOffspring", {"start": v(-26.48, -16.2) * mm, "mid": v(-25.05, -18.24) * mm, "end": v(-23.46, -20.17) * mm});
            skArc(sketch, "E134.trimOffspring", {"start": v(31.49, -15.1) * mm, "mid": v(35.45, 1.09) * mm, "end": v(31.49, 17.27) * mm});
            skSolve(sketch);
        }
        {
            var Q0;
            Q0 = qSketchRegion(id + "F14", true);
            extrude(context, id + "F15", {"entities" : qUnion([Q0]), "depth" : 1.02 * mm, "offsetDistance" : 25.4 * mm});
        }
        {
            var Q0;
            Q0=makeQuery(id+"F1.opExtrude","CAP_FACE",FACE,{"disambiguationData":[OSD([sQuery(id+"F0.wireOp",EDGE,"E10")])],"isStart":false});
            var sketch = newSketch(context, id + "F16", { "sketchPlane" : qUnion([Q0])});
            skPoint(sketch, "E135", {"position": v(0, 0) * mm});
            skSolve(sketch);
        }
        {
            var Q0;
            Q0=makeQuery(id+"F15.opExtrude","SWEPT_BODY",BODY,{"disambiguationData":[OSD([sQuery(id+"F14.wireOp",EDGE,"E45"),sQuery(id+"F14.wireOp",EDGE,"E46"),sQuery(id+"F14.wireOp",EDGE,"E47.left"),sQuery(id+"F14.wireOp",EDGE,"E47.right"),sQuery(id+"F14.wireOp",EDGE,"E48.1.0"),sQuery(id+"F14.wireOp",EDGE,"E48.1.1"),sQuery(id+"F14.wireOp",EDGE,"E48.2.0"),sQuery(id+"F14.wireOp",EDGE,"E48.2.1"),sQuery(id+"F14.wireOp",EDGE,"E50"),sQuery(id+"F14.wireOp",EDGE,"E54.trimOffspring"),sQuery(id+"F14.wireOp",EDGE,"E55.trimOffspring"),sQuery(id+"F14.wireOp",EDGE,"E62.trimOffspring"),sQuery(id+"F14.wireOp",EDGE,"E64.trimOffspring"),sQuery(id+"F14.wireOp",EDGE,"E65.trimOffspring"),sQuery(id+"F14.wireOp",EDGE,"E67.trimOffspring"),sQuery(id+"F14.wireOp",EDGE,"E71.trimOffspring"),sQuery(id+"F14.wireOp",EDGE,"E72.trimOffspring"),sQuery(id+"F14.wireOp",EDGE,"E74.trimOffspring"),sQuery(id+"F14.wireOp",EDGE,"E77.trimOffspring"),sQuery(id+"F14.wireOp",EDGE,"E82.trimOffspring"),sQuery(id+"F14.wireOp",EDGE,"E83.trimOffspring"),sQuery(id+"F14.wireOp",EDGE,"E84.trimOffspring"),sQuery(id+"F14.wireOp",EDGE,"E87.trimOffspring"),sQuery(id+"F14.wireOp",EDGE,"E95.trimOffspring"),sQuery(id+"F14.wireOp",EDGE,"E97.trimOffspring"),sQuery(id+"F14.wireOp",EDGE,"E98"),sQuery(id+"F14.wireOp",EDGE,"E99.bottom"),sQuery(id+"F14.wireOp",EDGE,"E99.top"),sQuery(id+"F14.wireOp",EDGE,"E100"),sQuery(id+"F14.wireOp",EDGE,"E101"),sQuery(id+"F14.wireOp",EDGE,"E102"),sQuery(id+"F14.wireOp",EDGE,"E103"),sQuery(id+"F14.wireOp",EDGE,"E104.1.0"),sQuery(id+"F14.wireOp",EDGE,"E104.1.1"),sQuery(id+"F14.wireOp",EDGE,"E104.1.2"),sQuery(id+"F14.wireOp",EDGE,"E104.1.3"),sQuery(id+"F14.wireOp",EDGE,"E104.1.4"),sQuery(id+"F14.wireOp",EDGE,"E104.1.5"),sQuery(id+"F14.wireOp",EDGE,"E104.2.0"),sQuery(id+"F14.wireOp",EDGE,"E104.2.1"),sQuery(id+"F14.wireOp",EDGE,"E104.2.2"),sQuery(id+"F14.wireOp",EDGE,"E104.2.3"),sQuery(id+"F14.wireOp",EDGE,"E104.2.4"),sQuery(id+"F14.wireOp",EDGE,"E104.2.5"),sQuery(id+"F14.wireOp",EDGE,"E105.trimOffspring"),sQuery(id+"F14.wireOp",EDGE,"E106.trimOffspring"),sQuery(id+"F14.wireOp",EDGE,"E107.trimOffspring"),sQuery(id+"F14.wireOp",EDGE,"E108.trimOffspring"),sQuery(id+"F14.wireOp",EDGE,"E109.trimOffspring"),sQuery(id+"F14.wireOp",EDGE,"E110"),sQuery(id+"F14.wireOp",EDGE,"E111"),sQuery(id+"F14.wireOp",EDGE,"E112"),sQuery(id+"F14.wireOp",EDGE,"E113"),sQuery(id+"F14.wireOp",EDGE,"E114"),sQuery(id+"F14.wireOp",EDGE,"E115"),sQuery(id+"F14.wireOp",EDGE,"E116.converted"),sQuery(id+"F14.wireOp",EDGE,"E117.trimOffspring"),sQuery(id+"F14.wireOp",EDGE,"E118.trimOffspring"),sQuery(id+"F14.wireOp",EDGE,"E119.trimOffspring"),sQuery(id+"F14.wireOp",EDGE,"E120.trimOffspring"),sQuery(id+"F14.wireOp",EDGE,"E121.trimOffspring"),sQuery(id+"F14.wireOp",EDGE,"E122.trimOffspring"),sQuery(id+"F14.wireOp",EDGE,"E123.trimOffspring"),sQuery(id+"F14.wireOp",EDGE,"E124.trimOffspring"),sQuery(id+"F14.wireOp",EDGE,"E125.trimOffspring"),sQuery(id+"F14.wireOp",EDGE,"E126.trimOffspring"),sQuery(id+"F14.wireOp",EDGE,"E127.trimOffspring"),sQuery(id+"F14.wireOp",EDGE,"E128.trimOffspring"),sQuery(id+"F14.wireOp",EDGE,"E129.trimOffspring"),sQuery(id+"F14.wireOp",EDGE,"E130.trimOffspring"),sQuery(id+"F14.wireOp",EDGE,"E131.trimOffspring"),sQuery(id+"F14.wireOp",EDGE,"E132.trimOffspring"),sQuery(id+"F14.wireOp",EDGE,"E133.trimOffspring"),sQuery(id+"F14.wireOp",EDGE,"E134.trimOffspring")])]});
            var Q1;
            Q1=sQuery(id+"F16.wireOp",VERTEX,"E135");
            transform(context, id + "F17", {"entities" : qUnion([Q0]), "transformType" : TransformType.SCALE_UNIFORMLY, "scale" : .7, "scalePoint" : qUnion([Q1]), "makeCopy" : false});
        }
    });
